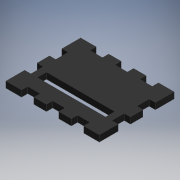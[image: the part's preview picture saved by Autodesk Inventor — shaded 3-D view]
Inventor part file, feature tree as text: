
AUTODESK INVENTOR PART (.ipt)
format: ipt  version: 2019 (Build 230136000, 136)  size: 178,176 bytes
history: native  units: mm
features: extrude x2, sketch x2, projected_geometry x1
ambient origin geometry x8: Origin, YZ Plane, XZ Plane, XY Plane, X Axis, Y Axis, Z Axis, Center Point
bodies: Solid1 (feature_tree)
feature tree (5):
  extrude  "Extrusion1"  Depth=48.0mm
  extrude  "Extrusion2"  Depth=4.0mm
  sketch  "Sketch1"  dims[d0=60.0mm d1=48.0mm]
  sketch  "Sketch2"  dims[d2=4.0mm d3=0.0mm d4=4.0mm d7=8.0mm d8=8.0mm d9=4.0mm d10=8.0mm d11=4.0mm d12=4.0mm d13=0.0mm d14=44.0mm d15=6.0mm d16=8.0mm d17=12.0mm]
  projected_geometry  "Projected Loop1"
